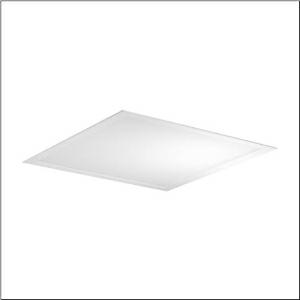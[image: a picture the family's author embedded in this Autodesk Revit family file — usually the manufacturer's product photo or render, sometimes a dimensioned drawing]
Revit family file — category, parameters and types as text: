
# Revit family: apollon_r__21_square_51mq11w72313_e9b2
name_source: partatom
category: Lighting Fixtures
units: mm (PartAtom-declared; Revit-internal decimal feet)

## family parameters
Cut with Voids When Loaded = No
Host = Face
Light Source = No
Part Type = Normal
Room Calculation Point = No
Round Connector Dimension = Use Diameter
Shared = No

## types (1)
- Apollon® 21 square (1 x LED, 4000 lm, 33 W, 3000K)
    Apparent Load = 33 VA
    CIE Flux Codes = 61 87 97 100 100
    Color Rendering = 80
    Color Temperature = 3000K
    Default Elevation = 1800 mm
    Description = Apollon® 21 square, office luminaire, primary optical cover: micro prismatic cover, of PMMA, CAT 2 (L<= 3000cd/m²), light emission: direct distribution, primary light characteristic: symmetric, installation type: lay-in mounting, LED, rated luminous flux: 4.000lm, luminous efficacy: 121lm/W, light colour: 830, colour temperature: 3000K, control gear: ECG, with terminal, 3-pole, mains connection: 220..240V, AC, 50/60Hz, rated input power: 33W, housing, of aluminium, traffic white (RAL 9016), module: M625, length: 620mm, width: 620mm, height: 40mm, housing upper side, of sheet steel, galvanised, protection rating (complete): IP20, protection rating (lamp compartment, on room side): IP50, insulation class (complete): insulation class II (safety insulation), certification: CE, ENEC, permissible operating ambient temperature: -20..+40°C, packaging unit: 1 piece
    Height = 0 mm  [stored 0 ft]
    Lamp = 1 x LED
    Lamp Light Flux = 4000 lm
    Lamp Power = 33 W
    Lamp count = 1
    Length = 620 mm
    Luminous efficacy = 121 lm/W
    Manufacturer = Siteco
    ModVariant = No
    Model = 51MQ11W72313
    Mounting Place = Ceiling
    Mounting Type = Recessed
    Number of Poles = 1
    OnlyDefault = Yes
    Power Factor = 1
    Product Name = Apollon® 21 square
    Product group = office luminaire | ceiling recessed
    ProductGroupID = 400
    Protection Class = Protection class II
    Protection Degree = IP 20
    RLX_Detail_Level = 1
    RlxData = <blob elided: 14889 chars, md5=9822fcbe>
    Socket = socket
    Standby Power = 0 W
    System Light Flux = 4000 lm
    System Power = 33 W
    Type Comments = Product without accessories
    Type Image = l_1006122.jpg
    URL = http://relux.com
    VarID = ---
    Voltage = 0 V
    Weight = 0.00 kg
    Width = 620 mm

note: [stored X ft] marks values corroborated as IEEE doubles in the binary element streams (Revit-internal decimal feet)

## geometry (parser evidence)
native form markers: Sweep x10
no freeform markers — native parametric forms only
